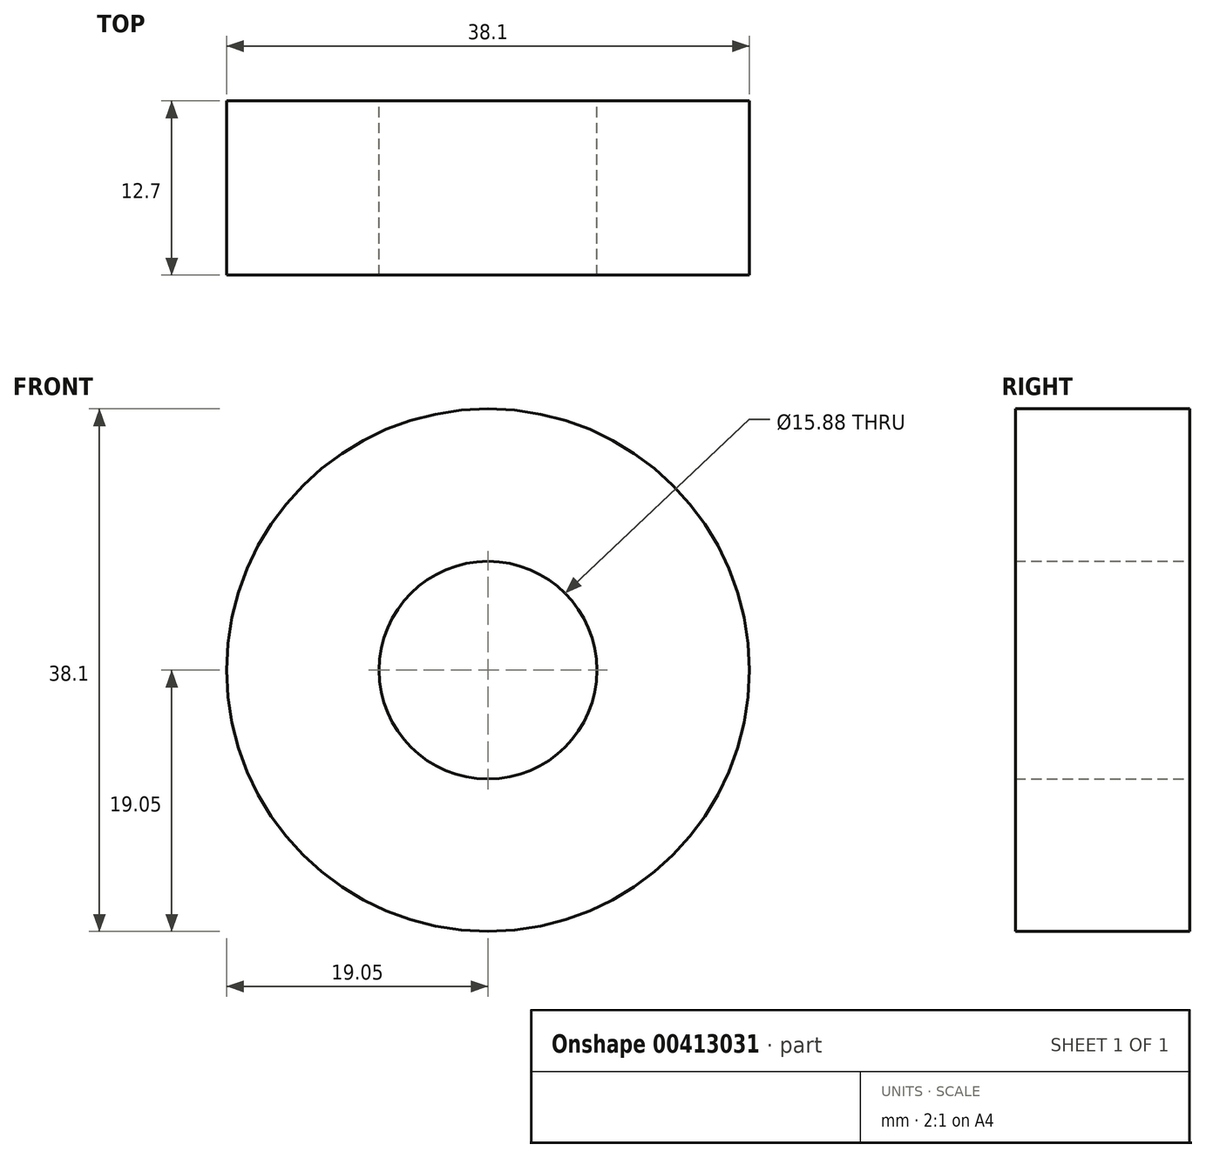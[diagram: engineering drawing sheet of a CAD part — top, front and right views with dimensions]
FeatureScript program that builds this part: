
annotation { "Feature Type Name" : "Feature", "Feature Type Description" : "" }
export const myFeature = defineFeature(function(context is Context, id is Id, definition is map)
    precondition{}
    {
        {
            var Q0;
            Q0=qCreatedBy(makeId("Front.planeOp"),FACE);
            var sketch = newSketch(context, id + "F0", { "sketchPlane" : qUnion([Q0])});
            skCircle(sketch, "E0", {"center": v(0, 0) * mm, "radius": 12.7 * mm});
            skCircle(sketch, "E1", {"center": v(0, 0) * mm, "radius": 19.05 * mm});
            skArc(sketch, "E2", {"start": v(0, -19.05) * mm, "mid": v(-17.4, -13.86) * mm, "end": v(-29.1, 0) * mm});
            skLineSegment(sketch, "E3", {"start": v(-29.1, 0) * mm, "end": v(-19.05, 0) * mm});
            skCircle(sketch, "E4", {"center": v(0, 0) * mm, "radius": 7.94 * mm});
            skSolve(sketch);
        }
        {
            var Q0;
            Q0=makeQuery(id+"F0.imprint","IMPRINT",FACE,{"disambiguationData":[TD([[makeQuery(id+"F0.imprint","IMPRINT",EDGE,{"derivedFrom":sQuery(id+"F0.wireOp",EDGE,"E0")}),1.0]])]});
            var Q1;
            Q1=makeQuery(id+"F0.imprint","IMPRINT",FACE,{"disambiguationData":[TD([[makeQuery(id+"F0.imprint","IMPRINT",EDGE,{"derivedFrom":sQuery(id+"F0.wireOp",EDGE,"E0")}),-1.0]])]});
            var Q2;
            {var subQ0=sQuery(id+"F0.wireOp",EDGE,"E2");Q2=makeQuery(id+"F0.imprint","IMPRINT",FACE,{"disambiguationData":[TD([[makeQuery(id+"F0.imprint","IMPRINT",EDGE,{"derivedFrom":subQ0}),-1.0]])]});}
            extrude(context, id + "F1", {"entities" : qUnion([Q0, Q1, Q2]), "depth" : 12.7 * mm});
        }
        {
            var Q0;
            Q0=makeQuery(id+"F1.opExtrude","CAP_FACE",FACE,{"disambiguationData":[OSD([sQuery(id+"F0.wireOp",EDGE,"E1"),sQuery(id+"F0.wireOp",EDGE,"E2"),sQuery(id+"F0.wireOp",EDGE,"E3"),sQuery(id+"F0.wireOp",EDGE,"E4")])],"isStart":false});
            var sketch = newSketch(context, id + "F2", { "sketchPlane" : qUnion([Q0])});
            skPoint(sketch, "E5", {"position": v(-24.07, -2.74) * mm});
            skPoint(sketch, "E5.positionSnap0", {"position": v(-24.07, 0) * mm});
            skSolve(sketch);
        }
        {
            var Q0;
            Q0=sQuery(id+"F2.wireOp",VERTEX,"E5");
            var Q1;
            Q1=makeQuery(id+"F1.opExtrude","SWEPT_BODY",BODY,{"disambiguationData":[OSD([sQuery(id+"F0.wireOp",EDGE,"E1"),sQuery(id+"F0.wireOp",EDGE,"E2"),sQuery(id+"F0.wireOp",EDGE,"E3"),sQuery(id+"F0.wireOp",EDGE,"E4")])]});
            hole(context, id + "F3", {"style" : HoleStyle.C_BORE, "endStyle" : HoleEndStyle.BLIND, "holeDiameter" : 1.59 * mm, "cBoreDiameter" : 1.59 * mm, "cBoreDepth" : 6.35 * mm, "holeDepth" : 25.4 * mm, "isTappedThrough" : true, "tappedDepth" : 12.7 * mm, "tapClearance" : 3, "locations" : qUnion([Q0]), "scope" : qUnion([Q1])});
        }
    });
